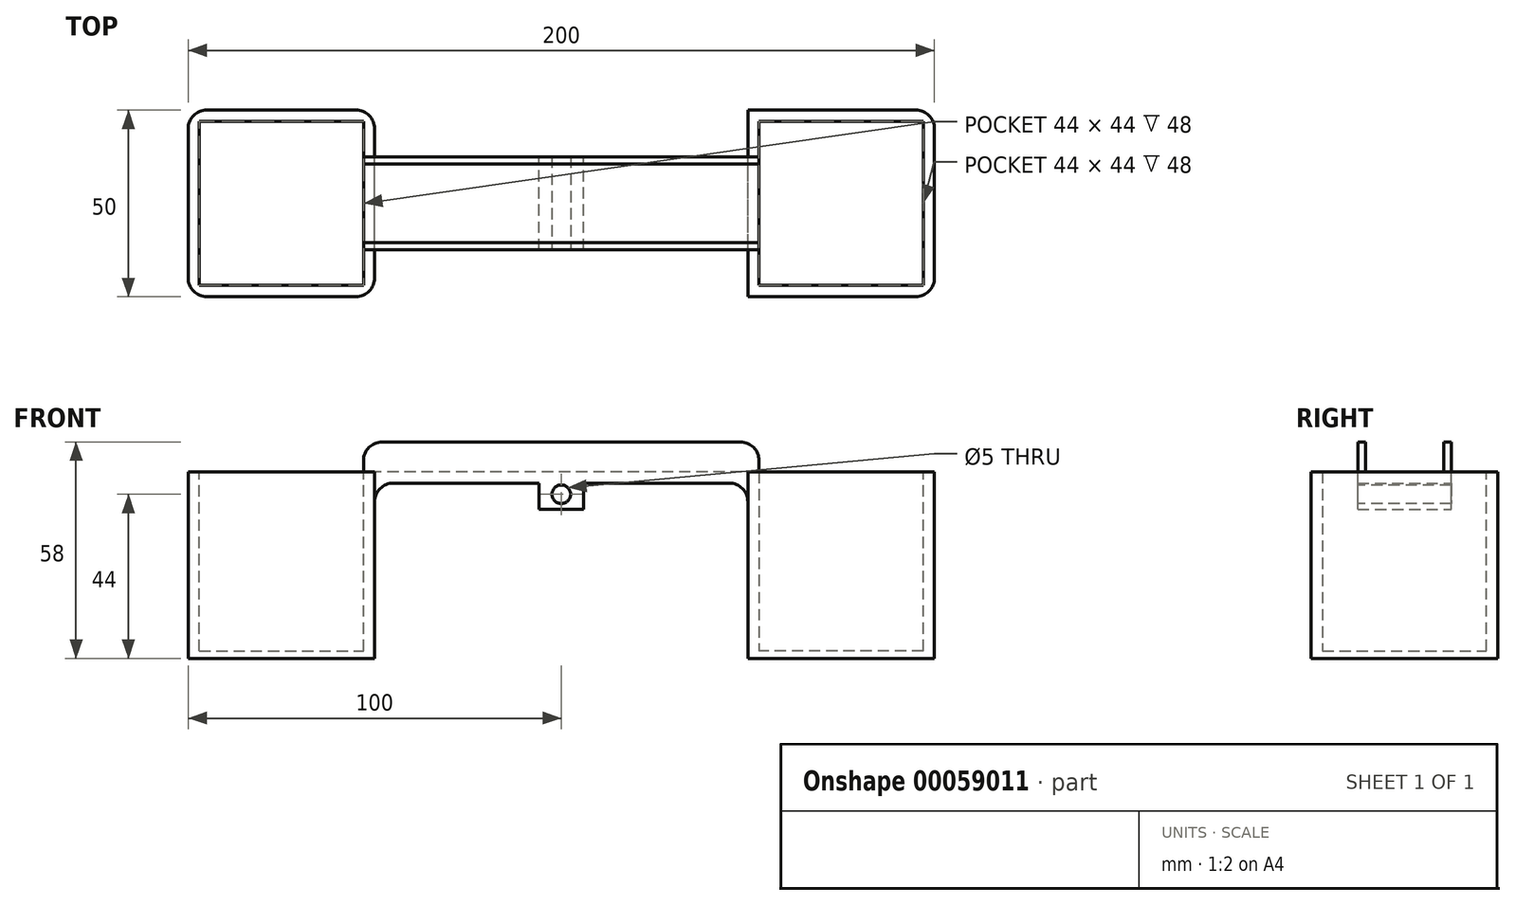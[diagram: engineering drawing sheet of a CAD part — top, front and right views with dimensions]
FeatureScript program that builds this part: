
annotation { "Feature Type Name" : "Feature", "Feature Type Description" : "" }
export const myFeature = defineFeature(function(context is Context, id is Id, definition is map)
    precondition{}
    {
        {
            var Q0;
            Q0=qCreatedBy(makeId("Front.planeOp"),FACE);
            var sketch = newSketch(context, id + "F0", { "sketchPlane" : qUnion([Q0])});
            skLineSegment(sketch, "E0.rect.bottom", {"start": v(-50, 1.5) * mm, "end": v(-6, 1.5) * mm});
            skLineSegment(sketch, "E0.rect.top", {"start": v(-50, -1.5) * mm, "end": v(-6, -1.5) * mm});
            skPoint(sketch, "E0.rect.middle", {"position": v(0, 0) * mm});
            skLineSegment(sketch, "E1.top", {"start": v(50, -48.5) * mm, "end": v(100, -48.5) * mm});
            skLineSegment(sketch, "E1.left", {"start": v(50, -1.5) * mm, "end": v(50, -48.5) * mm});
            skLineSegment(sketch, "E1.right", {"start": v(100, -1.5) * mm, "end": v(100, -48.5) * mm});
            skLineSegment(sketch, "E2.top", {"start": v(53, -46.5) * mm, "end": v(97, -46.5) * mm});
            skLineSegment(sketch, "E2.left", {"start": v(53, 1.5) * mm, "end": v(53, -46.5) * mm});
            skLineSegment(sketch, "E2.right", {"start": v(97, 1.5) * mm, "end": v(97, -46.5) * mm});
            skLineSegment(sketch, "E3", {"start": v(50, 1.5) * mm, "end": v(53, 1.5) * mm});
            skLineSegment(sketch, "E4", {"start": v(97, 1.5) * mm, "end": v(100, 1.5) * mm});
            skLineSegment(sketch, "E5", {"start": v(100, 1.5) * mm, "end": v(100, -1.5) * mm});
            skLineSegment(sketch, "E6.MirrorCS", {"start": v(-50, 1.5) * mm, "end": v(-53, 1.5) * mm});
            skLineSegment(sketch, "E7.MirrorCS", {"start": v(-100, 1.5) * mm, "end": v(-100, -1.5) * mm});
            skLineSegment(sketch, "E8.MirrorCS", {"start": v(-97, 1.5) * mm, "end": v(-100, 1.5) * mm});
            skLineSegment(sketch, "E9.MirrorCS", {"start": v(-50, -48.5) * mm, "end": v(-100, -48.5) * mm});
            skLineSegment(sketch, "E10.MirrorCS", {"start": v(-100, -1.5) * mm, "end": v(-100, -48.5) * mm});
            skLineSegment(sketch, "E11.MirrorCS", {"start": v(-53, -46.5) * mm, "end": v(-97, -46.5) * mm});
            skLineSegment(sketch, "E12.MirrorCS", {"start": v(-53, 1.5) * mm, "end": v(-53, -46.5) * mm});
            skLineSegment(sketch, "E13.MirrorCS", {"start": v(-50, -1.5) * mm, "end": v(-50, -48.5) * mm});
            skLineSegment(sketch, "E14.MirrorCS", {"start": v(-97, 1.5) * mm, "end": v(-97, -46.5) * mm});
            skPoint(sketch, "E15.MirrorCS.end.orphan", {"position": v(-50, -1.5) * mm});
            skPoint(sketch, "E15.MirrorCS.start.orphan", {"position": v(-50, 1.5) * mm});
            skLineSegment(sketch, "E16.trimOffspring", {"start": v(6, 1.5) * mm, "end": v(50, 1.5) * mm});
            skLineSegment(sketch, "E17.trimOffspring", {"start": v(6, -1.5) * mm, "end": v(50, -1.5) * mm});
            skLineSegment(sketch, "E18.rect.top", {"start": v(6, -8.5) * mm, "end": v(-6, -8.5) * mm});
            skLineSegment(sketch, "E19.trimOffspring", {"start": v(-6, -1.5) * mm, "end": v(-6, -8.5) * mm});
            skLineSegment(sketch, "E20.trimOffspring", {"start": v(6, -1.5) * mm, "end": v(6, -8.5) * mm});
            skLineSegment(sketch, "E21", {"start": v(-6, 1.5) * mm, "end": v(6, 1.5) * mm});
            skPoint(sketch, "E18.rect.bottom.end.orphan", {"position": v(-6, 8.5) * mm});
            skPoint(sketch, "E18.rect.left.start.orphan", {"position": v(6, 8.5) * mm});
            skSolve(sketch);
        }
        {
            var Q0;
            Q0 = qSketchRegion(id + "F0", true);
            extrude(context, id + "F1", {"entities" : qUnion([Q0]), "endBound" : BoundingType.SYMMETRIC, "depth" : 50 * mm});
        }
        {
            var Q0;
            Q0=makeQuery(id+"F1.opExtrude","CAP_FACE",FACE,{"disambiguationData":[OSD([sQuery(id+"F0.wireOp",EDGE,"E0.rect.bottom"),sQuery(id+"F0.wireOp",EDGE,"E0.rect.top"),sQuery(id+"F0.wireOp",EDGE,"5aaf5f09-95b2-4fc9-a8ba-4105307f4cd7"),sQuery(id+"F0.wireOp",EDGE,"E1.top"),sQuery(id+"F0.wireOp",EDGE,"E1.left"),sQuery(id+"F0.wireOp",EDGE,"E1.right"),sQuery(id+"F0.wireOp",EDGE,"E2.top"),sQuery(id+"F0.wireOp",EDGE,"E2.left"),sQuery(id+"F0.wireOp",EDGE,"E2.right"),sQuery(id+"F0.wireOp",EDGE,"E3"),sQuery(id+"F0.wireOp",EDGE,"E4"),sQuery(id+"F0.wireOp",EDGE,"E5"),sQuery(id+"F0.wireOp",EDGE,"E6.MirrorCS"),sQuery(id+"F0.wireOp",EDGE,"E7.MirrorCS"),sQuery(id+"F0.wireOp",EDGE,"E8.MirrorCS"),sQuery(id+"F0.wireOp",EDGE,"E9.MirrorCS"),sQuery(id+"F0.wireOp",EDGE,"E10.MirrorCS"),sQuery(id+"F0.wireOp",EDGE,"E11.MirrorCS"),sQuery(id+"F0.wireOp",EDGE,"E12.MirrorCS"),sQuery(id+"F0.wireOp",EDGE,"E13.MirrorCS"),sQuery(id+"F0.wireOp",EDGE,"E14.MirrorCS")])],"isStart":false});
            var sketch = newSketch(context, id + "F2", { "sketchPlane" : qUnion([Q0])});
            skLineSegment(sketch, "E22.bottom", {"start": v(100, 1.5) * mm, "end": v(50, 1.5) * mm});
            skLineSegment(sketch, "E22.top", {"start": v(100, -48.5) * mm, "end": v(50, -48.5) * mm});
            skLineSegment(sketch, "E22.left", {"start": v(100, 1.5) * mm, "end": v(100, -48.5) * mm});
            skLineSegment(sketch, "E22.right", {"start": v(50, 1.5) * mm, "end": v(50, -48.5) * mm});
            skLineSegment(sketch, "E23.MirrorCS", {"start": v(-50, 1.5) * mm, "end": v(-50, -48.5) * mm});
            skLineSegment(sketch, "E24.MirrorCS", {"start": v(-100, 1.5) * mm, "end": v(-100, -48.5) * mm});
            skLineSegment(sketch, "E25.MirrorCS", {"start": v(-100, 1.5) * mm, "end": v(-50, 1.5) * mm});
            skLineSegment(sketch, "E26.MirrorCS", {"start": v(-100, -48.5) * mm, "end": v(-50, -48.5) * mm});
            skSolve(sketch);
        }
        {
            var Q0;
            Q0 = qSketchRegion(id + "F2", true);
            extrude(context, id + "F3", {"entities" : qUnion([Q0]), "operationType" : NewBodyOperationType.ADD, "oppositeDirection" : true, "depth" : 3 * mm});
        }
        {
            var Q0;
            Q0=makeQuery(id+"F1.opExtrude","CAP_FACE",FACE,{"disambiguationData":[OSD([sQuery(id+"F0.wireOp",EDGE,"E0.rect.bottom"),sQuery(id+"F0.wireOp",EDGE,"E0.rect.top"),sQuery(id+"F0.wireOp",EDGE,"5aaf5f09-95b2-4fc9-a8ba-4105307f4cd7"),sQuery(id+"F0.wireOp",EDGE,"E1.top"),sQuery(id+"F0.wireOp",EDGE,"E1.left"),sQuery(id+"F0.wireOp",EDGE,"E1.right"),sQuery(id+"F0.wireOp",EDGE,"E2.top"),sQuery(id+"F0.wireOp",EDGE,"E2.left"),sQuery(id+"F0.wireOp",EDGE,"E2.right"),sQuery(id+"F0.wireOp",EDGE,"E3"),sQuery(id+"F0.wireOp",EDGE,"E4"),sQuery(id+"F0.wireOp",EDGE,"E5"),sQuery(id+"F0.wireOp",EDGE,"E6.MirrorCS"),sQuery(id+"F0.wireOp",EDGE,"E7.MirrorCS"),sQuery(id+"F0.wireOp",EDGE,"E8.MirrorCS"),sQuery(id+"F0.wireOp",EDGE,"E9.MirrorCS"),sQuery(id+"F0.wireOp",EDGE,"E10.MirrorCS"),sQuery(id+"F0.wireOp",EDGE,"E11.MirrorCS"),sQuery(id+"F0.wireOp",EDGE,"E12.MirrorCS"),sQuery(id+"F0.wireOp",EDGE,"E13.MirrorCS"),sQuery(id+"F0.wireOp",EDGE,"E14.MirrorCS")])],"isStart":true});
            var sketch = newSketch(context, id + "F4", { "sketchPlane" : qUnion([Q0])});
            skLineSegment(sketch, "E27.bottom", {"start": v(-100, 1.5) * mm, "end": v(-50, 1.5) * mm});
            skLineSegment(sketch, "E27.top", {"start": v(-100, -48.5) * mm, "end": v(-50, -48.5) * mm});
            skLineSegment(sketch, "E27.left", {"start": v(-100, 1.5) * mm, "end": v(-100, -48.5) * mm});
            skLineSegment(sketch, "E27.right", {"start": v(-50, 1.5) * mm, "end": v(-50, -48.5) * mm});
            skLineSegment(sketch, "E28.MirrorCS", {"start": v(50, 1.5) * mm, "end": v(50, -48.5) * mm});
            skLineSegment(sketch, "E29.MirrorCS", {"start": v(100, 1.5) * mm, "end": v(100, -48.5) * mm});
            skLineSegment(sketch, "E30.MirrorCS", {"start": v(100, 1.5) * mm, "end": v(50, 1.5) * mm});
            skLineSegment(sketch, "E31.MirrorCS", {"start": v(100, -48.5) * mm, "end": v(50, -48.5) * mm});
            skSolve(sketch);
        }
        {
            var Q0;
            Q0 = qSketchRegion(id + "F4", true);
            extrude(context, id + "F5", {"entities" : qUnion([Q0]), "operationType" : NewBodyOperationType.ADD, "oppositeDirection" : true, "depth" : 3 * mm});
        }
        {
            var Q0;
            Q0=makeQuery(id+"F5.boolean.opBoolean","MERGE",FACE,{"derivedFrom":[makeQuery(id+"F3.boolean.opBoolean","MERGE",FACE,{"derivedFrom":[makeQuery(id+"F1.opExtrude","SWEPT_FACE",FACE,{"disambiguationData":[OSD([sQuery(id+"F0.wireOp",EDGE,"E0.rect.bottom"),sQuery(id+"F0.wireOp",EDGE,"E6.MirrorCS")])]}),makeQuery(id+"F1.opExtrude","SWEPT_FACE",FACE,{"disambiguationData":[OSD([sQuery(id+"F0.wireOp",EDGE,"E8.MirrorCS")])]}),makeQuery(id+"F3.opExtrude","SWEPT_FACE",FACE,{"disambiguationData":[OSD([sQuery(id+"F2.wireOp",EDGE,"E25.MirrorCS")])]})]}),makeQuery(id+"F5.opExtrude","SWEPT_FACE",FACE,{"disambiguationData":[OSD([sQuery(id+"F4.wireOp",EDGE,"E30.MirrorCS")])]})]});
            var sketch = newSketch(context, id + "F6", { "sketchPlane" : qUnion([Q0])});
            skLineSegment(sketch, "E32.bottom", {"start": v(50, 25) * mm, "end": v(-50, 25) * mm});
            skLineSegment(sketch, "E32.top", {"start": v(50, 12.5) * mm, "end": v(6.07, 12.5) * mm});
            skLineSegment(sketch, "E32.left", {"start": v(50, 25) * mm, "end": v(50, 12.5) * mm});
            skLineSegment(sketch, "E32.right", {"start": v(-50, 25) * mm, "end": v(-50, 12.5) * mm});
            skLineSegment(sketch, "E33.trimOffspring", {"start": v(-6, 12.5) * mm, "end": v(-50, 12.5) * mm});
            skLineSegment(sketch, "E34.MirrorCS", {"start": v(50, -25) * mm, "end": v(-50, -25) * mm});
            skLineSegment(sketch, "E35.MirrorCS", {"start": v(50, -25) * mm, "end": v(50, -12.5) * mm});
            skLineSegment(sketch, "E36.MirrorCS", {"start": v(-50, -25) * mm, "end": v(-50, -12.5) * mm});
            skLineSegment(sketch, "E37.MirrorCS", {"start": v(-6, -12.5) * mm, "end": v(-50, -12.5) * mm});
            skLineSegment(sketch, "E38.MirrorCS", {"start": v(50, -12.5) * mm, "end": v(6.07, -12.5) * mm});
            skLineSegment(sketch, "E39", {"start": v(-6, 12.5) * mm, "end": v(6.07, 12.5) * mm});
            skLineSegment(sketch, "E40", {"start": v(-6, -12.5) * mm, "end": v(6.07, -12.5) * mm});
            skPoint(sketch, "E41.MirrorCS.end.orphan", {"position": v(6.07, -17.5) * mm});
            skPoint(sketch, "E42.MirrorCS.end.orphan", {"position": v(-6, -17.5) * mm});
            skPoint(sketch, "E43.top.end.orphan", {"position": v(6.07, 17.5) * mm});
            skPoint(sketch, "E43.left.end.orphan", {"position": v(-6, 17.5) * mm});
            skSolve(sketch);
        }
        {
            var Q0;
            Q0 = qSketchRegion(id + "F6", true);
            extrude(context, id + "F7", {"entities" : qUnion([Q0]), "operationType" : NewBodyOperationType.REMOVE, "endBound" : BoundingType.SYMMETRIC, "oppositeDirection" : true, "depth" : 25 * mm});
        }
        {
            var Q0;
            Q0=makeQuery(id+"F1.opExtrude","SWEPT_EDGE",EDGE,{"disambiguationData":[OSD([sQuery(id+"F0.wireOp",EDGE,"E1.left"),sQuery(id+"F0.wireOp",EDGE,"E17.trimOffspring")])]});
            var Q1;
            Q1=makeQuery(id+"F1.opExtrude","SWEPT_EDGE",EDGE,{"disambiguationData":[OSD([sQuery(id+"F0.wireOp",EDGE,"E0.rect.top"),sQuery(id+"F0.wireOp",EDGE,"E13.MirrorCS")])]});
            fillet(context, id + "F8", {"entities" : qUnion([Q0, Q1]), "radius" : 5 * mm, "tangentPropagation" : true, "allowEdgeOverflow" : false});
        }
        {
            var Q0;
            Q0=makeQuery(id+"F5.boolean.opBoolean","MERGE",FACE,{"derivedFrom":[makeQuery(id+"F3.boolean.opBoolean","MERGE",FACE,{"derivedFrom":[makeQuery(id+"F1.opExtrude","SWEPT_FACE",FACE,{"disambiguationData":[OSD([sQuery(id+"F0.wireOp",EDGE,"E3"),sQuery(id+"F0.wireOp",EDGE,"E16.trimOffspring")])]}),makeQuery(id+"F1.opExtrude","SWEPT_FACE",FACE,{"disambiguationData":[OSD([sQuery(id+"F0.wireOp",EDGE,"E4")])]}),makeQuery(id+"F3.opExtrude","SWEPT_FACE",FACE,{"disambiguationData":[OSD([sQuery(id+"F2.wireOp",EDGE,"E22.bottom")])]})]}),makeQuery(id+"F5.opExtrude","SWEPT_FACE",FACE,{"disambiguationData":[OSD([sQuery(id+"F4.wireOp",EDGE,"E27.bottom")])]})]});
            var sketch = newSketch(context, id + "F9", { "sketchPlane" : qUnion([Q0])});
            skLineSegment(sketch, "E44.bottom", {"start": v(53, 12.5) * mm, "end": v(-53, 12.5) * mm});
            skLineSegment(sketch, "E44.top", {"start": v(53, 10.5) * mm, "end": v(-53, 10.5) * mm});
            skLineSegment(sketch, "E44.left", {"start": v(53, 12.5) * mm, "end": v(53, 10.5) * mm});
            skLineSegment(sketch, "E44.right", {"start": v(-53, 12.5) * mm, "end": v(-53, 10.5) * mm});
            skLineSegment(sketch, "E45.MirrorCS", {"start": v(53, -12.5) * mm, "end": v(53, -10.5) * mm});
            skLineSegment(sketch, "E46.MirrorCS", {"start": v(-53, -12.5) * mm, "end": v(-53, -10.5) * mm});
            skLineSegment(sketch, "E47.MirrorCS", {"start": v(53, -12.5) * mm, "end": v(-53, -12.5) * mm});
            skLineSegment(sketch, "E48.MirrorCS", {"start": v(53, -10.5) * mm, "end": v(-53, -10.5) * mm});
            skSolve(sketch);
        }
        {
            var Q0;
            Q0 = qSketchRegion(id + "F9", true);
            extrude(context, id + "F10", {"entities" : qUnion([Q0]), "operationType" : NewBodyOperationType.ADD, "depth" : 8 * mm});
        }
        {
            var Q0;
            Q0=makeQuery(id+"F7.boolean.opBoolean","MERGE",EDGE,{"derivedFrom":[makeQuery(id+"F1.opExtrude","CAP_EDGE",EDGE,{"disambiguationData":[OSD([sQuery(id+"F0.wireOp",EDGE,"E13.MirrorCS")])],"isStart":false}),makeQuery(id+"F7.opExtrude","SWEPT_EDGE",EDGE,{"disambiguationData":[OSD([sQuery(id+"F0.wireOp",EDGE,"E0.rect.bottom"),sQuery(id+"F0.wireOp",EDGE,"E6.MirrorCS"),sQuery(id+"F0.wireOp",EDGE,"E8.MirrorCS"),sQuery(id+"F2.wireOp",EDGE,"E25.MirrorCS"),sQuery(id+"F6.wireOp",EDGE,"E34.MirrorCS"),sQuery(id+"F6.wireOp",EDGE,"E36.MirrorCS")])]})]});
            var Q1;
            Q1=makeQuery(id+"F1.opExtrude","CAP_EDGE",EDGE,{"disambiguationData":[OSD([sQuery(id+"F0.wireOp",EDGE,"E7.MirrorCS"),sQuery(id+"F0.wireOp",EDGE,"E10.MirrorCS")])],"isStart":false});
            var Q2;
            Q2=makeQuery(id+"F1.opExtrude","CAP_EDGE",EDGE,{"disambiguationData":[OSD([sQuery(id+"F0.wireOp",EDGE,"E7.MirrorCS"),sQuery(id+"F0.wireOp",EDGE,"E10.MirrorCS")])],"isStart":true});
            var Q3;
            Q3=makeQuery(id+"F7.boolean.opBoolean","MERGE",EDGE,{"derivedFrom":[makeQuery(id+"F1.opExtrude","CAP_EDGE",EDGE,{"disambiguationData":[OSD([sQuery(id+"F0.wireOp",EDGE,"E13.MirrorCS")])],"isStart":true}),makeQuery(id+"F7.opExtrude","SWEPT_EDGE",EDGE,{"disambiguationData":[OSD([sQuery(id+"F0.wireOp",EDGE,"E0.rect.bottom"),sQuery(id+"F0.wireOp",EDGE,"E6.MirrorCS"),sQuery(id+"F0.wireOp",EDGE,"E8.MirrorCS"),sQuery(id+"F4.wireOp",EDGE,"E30.MirrorCS"),sQuery(id+"F6.wireOp",EDGE,"E32.bottom"),sQuery(id+"F6.wireOp",EDGE,"E32.right")])]})]});
            var Q4;
            Q4=makeQuery(id+"F1.opExtrude","CAP_EDGE",EDGE,{"disambiguationData":[OSD([sQuery(id+"F0.wireOp",EDGE,"E1.right"),sQuery(id+"F0.wireOp",EDGE,"E5")])],"isStart":false});
            var Q5;
            Q5=makeQuery(id+"F7.boolean.opBoolean","MERGE",EDGE,{"derivedFrom":[makeQuery(id+"F1.opExtrude","CAP_EDGE",EDGE,{"disambiguationData":[OSD([sQuery(id+"F0.wireOp",EDGE,"E1.left")])],"isStart":false}),makeQuery(id+"F7.opExtrude","SWEPT_EDGE",EDGE,{"disambiguationData":[OSD([sQuery(id+"F6.wireOp",EDGE,"E34.MirrorCS"),sQuery(id+"F6.wireOp",EDGE,"E35.MirrorCS")])]})]});
            var Q6;
            Q6=makeQuery(id+"F1.opExtrude","CAP_EDGE",EDGE,{"disambiguationData":[OSD([sQuery(id+"F0.wireOp",EDGE,"E1.right"),sQuery(id+"F0.wireOp",EDGE,"E5")])],"isStart":true});
            var Q7;
            Q7=makeQuery(id+"F7.boolean.opBoolean","MERGE",EDGE,{"derivedFrom":[makeQuery(id+"F1.opExtrude","CAP_EDGE",EDGE,{"disambiguationData":[OSD([sQuery(id+"F0.wireOp",EDGE,"E1.left")])],"isStart":true}),makeQuery(id+"F7.opExtrude","SWEPT_EDGE",EDGE,{"disambiguationData":[OSD([sQuery(id+"F6.wireOp",EDGE,"E32.bottom"),sQuery(id+"F6.wireOp",EDGE,"E32.left")])]})]});
            fillet(context, id + "F11", {"entities" : qUnion([Q0, Q1, Q2, Q3, Q4, Q5, Q6, Q7]), "radius" : 5 * mm, "tangentPropagation" : true, "allowEdgeOverflow" : false});
        }
        {
            var Q0;
            Q0=makeQuery(id+"F10.opExtrude","CAP_EDGE",EDGE,{"disambiguationData":[OSD([sQuery(id+"F9.wireOp",EDGE,"E45.MirrorCS")])],"isStart":false});
            var Q1;
            Q1=makeQuery(id+"F10.opExtrude","CAP_EDGE",EDGE,{"disambiguationData":[OSD([sQuery(id+"F9.wireOp",EDGE,"E44.left")])],"isStart":false});
            var Q2;
            Q2=makeQuery(id+"F10.opExtrude","CAP_EDGE",EDGE,{"disambiguationData":[OSD([sQuery(id+"F9.wireOp",EDGE,"E46.MirrorCS")])],"isStart":false});
            var Q3;
            Q3=makeQuery(id+"F10.opExtrude","CAP_EDGE",EDGE,{"disambiguationData":[OSD([sQuery(id+"F9.wireOp",EDGE,"E44.right")])],"isStart":false});
            fillet(context, id + "F12", {"entities" : qUnion([Q0, Q1, Q2, Q3]), "radius" : 5 * mm, "tangentPropagation" : true, "allowEdgeOverflow" : false});
        }
        {
            var Q0;
            Q0=makeQuery(id+"F10.boolean.opBoolean","MERGE",FACE,{"derivedFrom":[makeQuery(id+"F7.boolean.opBoolean","COPY",FACE,{"derivedFrom":makeQuery(id+"F7.opExtrude","SWEPT_FACE",FACE,{"disambiguationData":[OSD([sQuery(id+"F6.wireOp",EDGE,"E37.MirrorCS"),sQuery(id+"F6.wireOp",EDGE,"E38.MirrorCS"),sQuery(id+"F6.wireOp",EDGE,"E40")])]})}),makeQuery(id+"F10.opExtrude","SWEPT_FACE",FACE,{"disambiguationData":[OSD([sQuery(id+"F9.wireOp",EDGE,"E47.MirrorCS")])]})]});
            var sketch = newSketch(context, id + "F13", { "sketchPlane" : qUnion([Q0])});
            skCircle(sketch, "E49", {"center": v(0, -4.5) * mm, "radius": 2.5 * mm});
            skSolve(sketch);
        }
        {
            var Q0;
            Q0=makeQuery(id+"F13.imprint","IMPRINT",FACE,{"disambiguationData":[TD([[makeQuery(id+"F13.imprint","IMPRINT",EDGE,{"derivedFrom":sQuery(id+"F13.wireOp",EDGE,"E49")}),1.0]])]});
            var Q1;
            Q1=sQuery(id+"F13.wireOp",EDGE,"73281b12-999f-4f59-8afc-c6d0f8b6b200");
            extrude(context, id + "F14", {"entities" : qUnion([Q0]), "operationType" : NewBodyOperationType.REMOVE, "surfaceEntities" : qUnion([Q1]), "endBound" : BoundingType.THROUGH_ALL, "oppositeDirection" : true, "depth" : 25 * mm});
        }
    });
